# Revit family: 931-20-001 DN80-200
name_source: partatom
category: Pipe Accessories
units: mm (PartAtom-declared; Revit-internal decimal feet)

## family parameters
Always vertical = Yes
Cut with Voids When Loaded = No
Part Type = Valve - Breaks Into
Round Connector Dimension = Use Diameter
Shared = No
Work Plane-Based = No

## types (5) — shared parameters
1 = 1 mm  [stored 0.00328084 ft]
2 = 3 mm  [stored 0.00984252 ft]
DN080_PN10/16 = 931-080-20-020040200000
DN100_PN10/16 = 931-100-20-020040200000
DN150_PN10/16 = 931-150-20-020040200000
DN200_PN10 = 931-200-20-010020200000
DN200_PN16 = 931-200-20-020020200000
Description_ = AVK BUTTERFLY VALVE, LUG, PN10/16
Search_table = 931-20-001 DN80-200
URL_product_pages = https://www.avkvalves.com
zero-valued in all types: DISK, Default Elevation

## per-type parameters (varying)
- DN080_PN10/16: Actuator_FL_T=19 mm  [stored 0.062336 ft]; Actuator_Flange_R=45 mm  [stored 0.147638 ft]; B=39 mm  [stored 0.127953 ft]; B1=40 mm  [stored 0.131234 ft]; Body_Thickness=6 mm  [stored 0.019685 ft]; Body_dim=23 mm  [stored 0.0754593 ft]; Body_dim1=32 mm  [stored 0.104987 ft]; Body_thickness=42 mm  [stored 0.137795 ft]; Bore_R=40 mm  [stored 0.131234 ft]; C=46 mm  [stored 0.150919 ft]; D=65 mm; DN=80 mm; E=159 mm; F=18 mm  [stored 0.0590551 ft]; Flange_R=97 mm; Flange_T=19 mm  [stored 0.062336 ft]; G=11 mm  [stored 0.0360892 ft]; H=45 mm  [stored 0.147638 ft]; Hole=12 mm  [stored 0.0393701 ft]; Hole1=14 mm  [stored 0.0459318 ft]; PCD_R=80 mm; Slot_dim=14 mm  [stored 0.0459318 ft]; base=16 mm  [stored 0.0524934 ft]; base1=9 mm  [stored 0.0295276 ft]; base_dis=77 mm; disk=5 mm  [stored 0.0164042 ft]; disk1=12 mm  [stored 0.0393701 ft]; disk11=16 mm  [stored 0.0524934 ft]; disk2=78 mm; disk22=7 mm  [stored 0.0229659 ft]; hole1=6 mm  [stored 0.019685 ft]; rubber=13 mm; support=88 mm; wafer=68 mm; wafer_F=16 mm  [stored 0.0524934 ft]; wafer_dim1=38 mm  [stored 0.124672 ft]; wafer_dim2=45 mm  [stored 0.147638 ft]; wafer_fillet=34 mm  [stored 0.111549 ft]
- DN100_PN10/16: Actuator_FL_T=19 mm  [stored 0.062336 ft]; Actuator_Flange_R=45 mm  [stored 0.147638 ft]; B=52 mm; B1=53 mm  [stored 0.173885 ft]; Body_Thickness=6 mm  [stored 0.019685 ft]; Body_dim=23 mm  [stored 0.0754593 ft]; Body_dim1=36 mm  [stored 0.11811 ft]; Body_thickness=56 mm; Bore_R=50 mm  [stored 0.164042 ft]; C=52 mm; D=81 mm; DN=100 mm; E=178 mm; F=22 mm  [stored 0.0721785 ft]; Flange_R=110 mm; Flange_T=19 mm  [stored 0.062336 ft]; G=11 mm  [stored 0.0360892 ft]; H=45 mm  [stored 0.147638 ft]; Hole=12 mm  [stored 0.0393701 ft]; Hole1=14 mm  [stored 0.0459318 ft]; PCD_R=90 mm; Slot_dim=14 mm  [stored 0.0459318 ft]; base=18 mm  [stored 0.0590551 ft]; base1=10 mm  [stored 0.0328084 ft]; base_dis=96 mm; disk=7 mm  [stored 0.0229659 ft]; disk1=12 mm  [stored 0.0393701 ft]; disk11=16 mm  [stored 0.0524934 ft]; disk2=104 mm; disk22=9 mm  [stored 0.0295276 ft]; hole1=6 mm  [stored 0.019685 ft]; rubber=16 mm  [stored 0.0524934 ft]; support=101 mm; wafer=68 mm; wafer_F=16 mm  [stored 0.0524934 ft]; wafer_dim1=35 mm  [stored 0.114829 ft]; wafer_dim2=50 mm  [stored 0.164042 ft]; wafer_fillet=34 mm  [stored 0.111549 ft]
- DN150_PN10/16: Actuator_FL_T=19 mm  [stored 0.062336 ft]; Actuator_Flange_R=45 mm  [stored 0.147638 ft]; B=74 mm; B1=75 mm; Body_Thickness=6 mm  [stored 0.019685 ft]; Body_dim=23 mm  [stored 0.0754593 ft]; Body_dim1=39 mm  [stored 0.127953 ft]; Body_thickness=79 mm; Bore_R=75 mm; C=56 mm; D=108 mm; DN=150 mm; E=203 mm; F=30 mm  [stored 0.0984252 ft]; Flange_R=143 mm; Flange_T=19 mm  [stored 0.062336 ft]; G=14 mm  [stored 0.0459318 ft]; H=45 mm  [stored 0.147638 ft]; Hole=15 mm  [stored 0.0492126 ft]; Hole1=18 mm  [stored 0.0590551 ft]; PCD_R=120 mm; Slot_dim=18 mm  [stored 0.0590551 ft]; base=20 mm  [stored 0.0656168 ft]; base1=11 mm  [stored 0.0360892 ft]; base_dis=127 mm; disk=8 mm  [stored 0.0262467 ft]; disk1=15 mm  [stored 0.0492126 ft]; disk11=20 mm  [stored 0.0656168 ft]; disk2=148 mm; disk22=10 mm  [stored 0.0328084 ft]; hole1=7 mm  [stored 0.0229659 ft]; rubber=17 mm  [stored 0.0557743 ft]; support=133 mm; wafer=68 mm; wafer_F=20 mm  [stored 0.0656168 ft]; wafer_dim1=28 mm  [stored 0.0918635 ft]; wafer_dim2=62 mm; wafer_fillet=34 mm  [stored 0.111549 ft]
- DN200_PN10: Actuator_FL_T=19 mm  [stored 0.062336 ft]; Actuator_Flange_R=63 mm; B=100 mm; B1=101 mm; Body_Thickness=7 mm  [stored 0.0229659 ft]; Body_dim=31 mm  [stored 0.101706 ft]; Body_dim1=42 mm  [stored 0.137795 ft]; Body_thickness=106 mm; Bore_R=100 mm; C=60 mm; D=136 mm; DN=200 mm; E=241 mm; F=30 mm  [stored 0.0984252 ft]; Flange_R=170 mm; Flange_T=19 mm  [stored 0.062336 ft]; G=17 mm  [stored 0.0557743 ft]; H=63 mm; Hole=19 mm  [stored 0.062336 ft]; Hole1=20 mm  [stored 0.0656168 ft]; PCD_R=148 mm; Slot_dim=18 mm  [stored 0.0590551 ft]; base=21 mm  [stored 0.0688976 ft]; base1=12 mm  [stored 0.0393701 ft]; base_dis=160 mm; disk=9 mm  [stored 0.0295276 ft]; disk1=17 mm  [stored 0.0557743 ft]; disk11=22 mm  [stored 0.0721785 ft]; disk2=199 mm; disk22=12 mm  [stored 0.0393701 ft]; hole1=9 mm  [stored 0.0295276 ft]; rubber=18 mm  [stored 0.0590551 ft]; support=170 mm; wafer=94 mm; wafer_F=20 mm  [stored 0.0656168 ft]; wafer_dim1=37 mm  [stored 0.121391 ft]; wafer_dim2=76 mm; wafer_fillet=47 mm
- DN200_PN16: Actuator_FL_T=20 mm  [stored 0.0656168 ft]; Actuator_Flange_R=63 mm; B=100 mm; B1=101 mm; Body_Thickness=7 mm  [stored 0.0229659 ft]; Body_dim=31 mm  [stored 0.101706 ft]; Body_dim1=42 mm  [stored 0.137795 ft]; Body_thickness=106 mm; Bore_R=100 mm; C=60 mm; D=136 mm; DN=200 mm; E=241 mm; F=30 mm  [stored 0.0984252 ft]; Flange_R=170 mm; Flange_T=20 mm  [stored 0.0656168 ft]; G=17 mm  [stored 0.0557743 ft]; H=63 mm; Hole=19 mm  [stored 0.062336 ft]; Hole1=17 mm  [stored 0.0557743 ft]; PCD_R=149 mm; Slot_dim=18 mm  [stored 0.0590551 ft]; base=21 mm  [stored 0.0688976 ft]; base1=12 mm  [stored 0.0393701 ft]; base_dis=160 mm; disk=10 mm  [stored 0.0328084 ft]; disk1=17 mm  [stored 0.0557743 ft]; disk11=22 mm  [stored 0.0721785 ft]; disk2=199 mm; disk22=13 mm; hole1=9 mm  [stored 0.0295276 ft]; rubber=18 mm  [stored 0.0590551 ft]; support=170 mm; wafer=94 mm; wafer_F=20 mm  [stored 0.0656168 ft]; wafer_dim1=37 mm  [stored 0.121391 ft]; wafer_dim2=76 mm; wafer_fillet=47 mm

note: [stored X ft] marks values corroborated as IEEE doubles in the binary element streams (Revit-internal decimal feet)

## geometry (parser evidence)
native form markers: Sweep x4
no freeform markers — native parametric forms only
